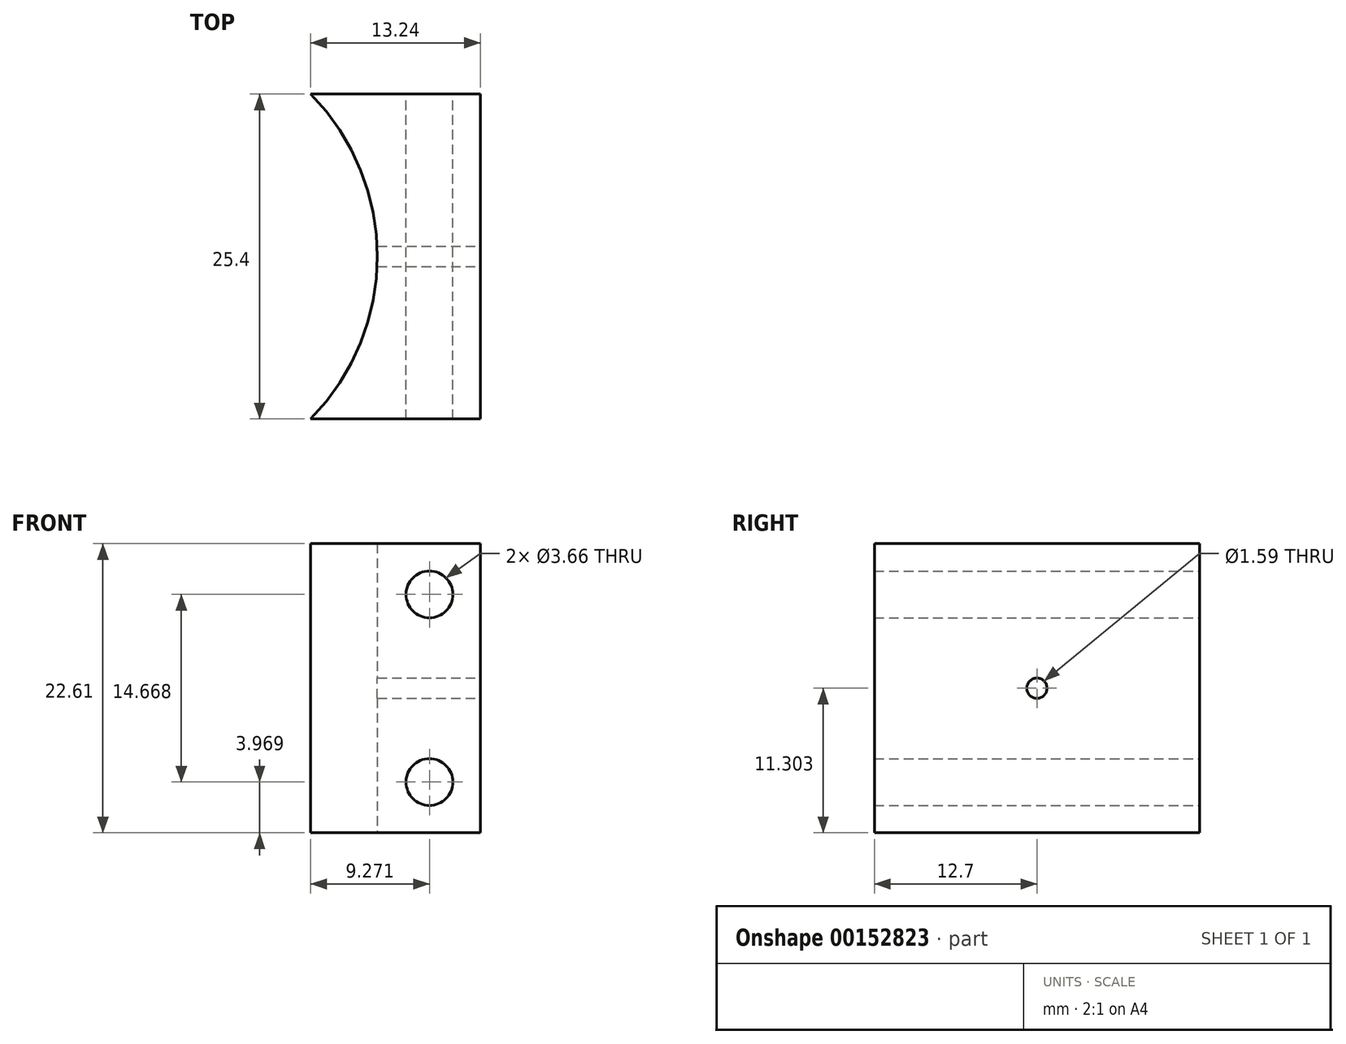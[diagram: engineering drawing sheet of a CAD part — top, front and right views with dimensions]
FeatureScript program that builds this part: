
annotation { "Feature Type Name" : "Feature", "Feature Type Description" : "" }
export const myFeature = defineFeature(function(context is Context, id is Id, definition is map)
    precondition{}
    {
        {
            var Q0;
            Q0=qCreatedBy(makeId("Top.planeOp"),FACE);
            var sketch = newSketch(context, id + "F0", { "sketchPlane" : qUnion([Q0])});
            skArc(sketch, "E0", {"start": v(0, 0) * mm, "mid": v(5.2, 12.7) * mm, "end": v(0, 25.4) * mm});
            skLineSegment(sketch, "E1", {"start": v(0, 0) * mm, "end": v(13.24, 0) * mm});
            skLineSegment(sketch, "E2", {"start": v(13.24, 0) * mm, "end": v(13.24, 25.4) * mm});
            skLineSegment(sketch, "E3", {"start": v(13.24, 25.4) * mm, "end": v(0, 25.4) * mm});
            skLineSegment(sketch, "E4", {"start": v(13.24, 12.7) * mm, "end": v(5.2, 12.7) * mm, "construction": true});
            skArc(sketch, "E5", {"start": v(0, 25.4) * mm, "mid": v(-12.9, 30.8) * mm, "end": v(-25.79, 25.4) * mm, "construction": true});
            skLineSegment(sketch, "E6", {"start": v(0, 25.4) * mm, "end": v(-12.9, 12.7) * mm, "construction": true});
            skLineSegment(sketch, "E7", {"start": v(-25.79, 25.4) * mm, "end": v(-12.9, 12.7) * mm, "construction": true});
            skLineSegment(sketch, "E8", {"start": v(-12.9, 12.7) * mm, "end": v(-12.9, 30.8) * mm, "construction": true});
            skLineSegment(sketch, "E9", {"start": v(-12.9, 12.7) * mm, "end": v(0, 0) * mm, "construction": true});
            skSolve(sketch);
        }
        {
            var Q0;
            Q0 = qSketchRegion(id + "F0", true);
            extrude(context, id + "F1", {"entities" : qUnion([Q0]), "depth" : 22.6 * mm});
        }
        {
            var Q0;
            Q0=makeQuery(id+"F1.opExtrude","SWEPT_FACE",FACE,{"disambiguationData":[OSD([sQuery(id+"F0.wireOp",EDGE,"E3")])]});
            var sketch = newSketch(context, id + "F2", { "sketchPlane" : qUnion([Q0])});
            skLineSegment(sketch, "E10.bottom", {"start": v(-13.24, 0) * mm, "end": v(-9.27, 0) * mm, "construction": true});
            skLineSegment(sketch, "E10.top", {"start": v(-13.24, 3.97) * mm, "end": v(-9.27, 3.97) * mm, "construction": true});
            skLineSegment(sketch, "E10.left", {"start": v(-13.24, 0) * mm, "end": v(-13.24, 3.97) * mm, "construction": true});
            skLineSegment(sketch, "E10.right", {"start": v(-9.27, 0) * mm, "end": v(-9.27, 3.97) * mm, "construction": true});
            skLineSegment(sketch, "E11.bottom", {"start": v(-13.24, 22.6) * mm, "end": v(-9.27, 22.6) * mm, "construction": true});
            skLineSegment(sketch, "E11.top", {"start": v(-13.24, 18.64) * mm, "end": v(-9.27, 18.64) * mm, "construction": true});
            skLineSegment(sketch, "E11.left", {"start": v(-13.24, 22.6) * mm, "end": v(-13.24, 18.64) * mm, "construction": true});
            skLineSegment(sketch, "E11.right", {"start": v(-9.27, 22.6) * mm, "end": v(-9.27, 18.64) * mm, "construction": true});
            skCircle(sketch, "E12", {"center": v(-9.27, 3.97) * mm, "radius": 1.83 * mm});
            skCircle(sketch, "E13", {"center": v(-9.27, 18.64) * mm, "radius": 1.83 * mm});
            skSolve(sketch);
        }
        {
            var Q0;
            Q0 = qSketchRegion(id + "F2", true);
            var Q1;
            Q1=makeQuery(id+"F1.opExtrude","SWEPT_FACE",FACE,{"disambiguationData":[OSD([sQuery(id+"F0.wireOp",EDGE,"E1")])]});
            extrude(context, id + "F3", {"entities" : qUnion([Q0]), "operationType" : NewBodyOperationType.REMOVE, "endBound" : BoundingType.UP_TO_SURFACE, "oppositeDirection" : true, "endBoundEntityFace" : qUnion([Q1]), "depth" : 25.4 * mm});
        }
        {
            var Q0;
            Q0=makeQuery(id+"F1.opExtrude","SWEPT_FACE",FACE,{"disambiguationData":[OSD([sQuery(id+"F0.wireOp",EDGE,"E2")])]});
            var sketch = newSketch(context, id + "F4", { "sketchPlane" : qUnion([Q0])});
            skLineSegment(sketch, "E14", {"start": v(25.4, 11.3) * mm, "end": v(0, 11.3) * mm, "construction": true});
            skCircle(sketch, "E15", {"center": v(12.7, 11.3) * mm, "radius": 0.8 * mm});
            skSolve(sketch);
        }
        {
            var Q0;
            Q0 = qSketchRegion(id + "F4", true);
            var Q1;
            Q1=makeQuery(id+"F1.opExtrude","SWEPT_FACE",FACE,{"disambiguationData":[OSD([sQuery(id+"F0.wireOp",EDGE,"E0")])]});
            extrude(context, id + "F5", {"entities" : qUnion([Q0]), "operationType" : NewBodyOperationType.REMOVE, "endBound" : BoundingType.UP_TO_SURFACE, "oppositeDirection" : true, "endBoundEntityFace" : qUnion([Q1]), "depth" : 25.4 * mm});
        }
    });
